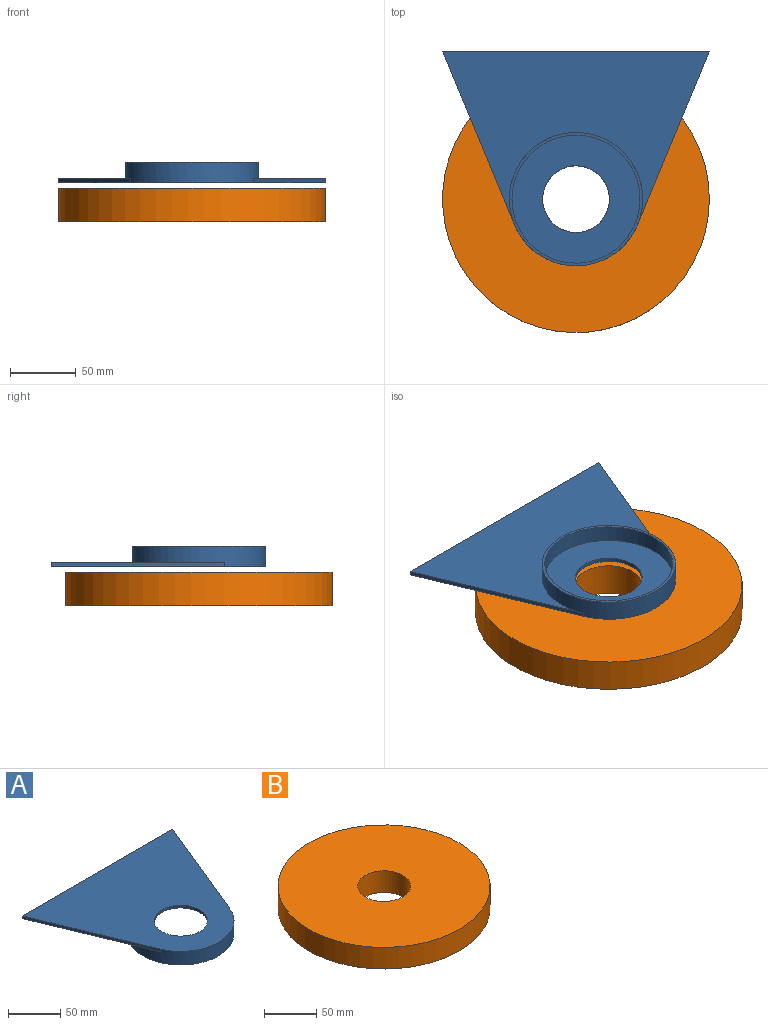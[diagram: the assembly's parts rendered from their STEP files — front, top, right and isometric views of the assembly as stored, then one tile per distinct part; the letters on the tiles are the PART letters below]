
ASSEMBLY  parts=2 mates=1
PART A: 10 faces, bbox 203.2x163.3x15.7 mm
  f0: plane 97.54x97.54mm, normal (0,0,-1), area 5444.9mm2, adj f4,f8
  f1: plane 131.98x54.67mm, normal (-0.92,-0.38,0), area 435.4mm2, adj f2,f5,f6,f7
  f2: cylinder r=50.8mm len=101.6mm, axis (0,0,1), area 4418.5mm2, adj f1,f3,f6,f7,f9
  f3: plane 131.98x54.67mm, normal (0.92,-0.38,0), area 435.4mm2, adj f2,f5,f6,f7
  f4: cylinder r=25.4mm len=50.8mm, axis (0,0,1), area 486.4mm2, adj f0,f7
  f5: plane 203.2x3.05mm, normal (0,1,0), area 619.4mm2, adj f1,f3,f6,f7
  f6: plane 203.2x131.98mm, normal (0,0,-1), area 13623.6mm2, adj f1,f2,f3,f5
  f7: plane 203.2x163.34mm, normal (0,0,1), area 19704.1mm2, adj f1,f2,f3,f4,f5
  f8: cylinder r=48.77mm len=97.54mm, axis (0,0,1), area 3891.5mm2, adj f0,f9
  f9: plane 101.6x101.6mm, normal (0,0,-1), area 635.6mm2, adj f2,f8
PART B: 4 faces, bbox 203.2x203.2x25.4 mm
  f0: cylinder r=25.4mm len=50.8mm, axis (0,0,-1), area 4053.7mm2, adj f2,f3
  f1: cylinder r=101.6mm len=203.2mm, axis (0,0,-1), area 16214.6mm2, adj f2,f3
  f2: plane 203.2x203.2mm, normal (0,0,1), area 30402.4mm2, adj f0,f1
  f3: plane 203.2x203.2mm, normal (0,0,-1), area 30402.4mm2, adj f0,f1
PLACE A rot(axis=(0,1,0),180deg) t=(0,0,16.76)mm
PLACE B at identity
MATE cylindrical A.f4 <-> B.f0  axis (0,0,-1) through (0,0,18.29)mm
